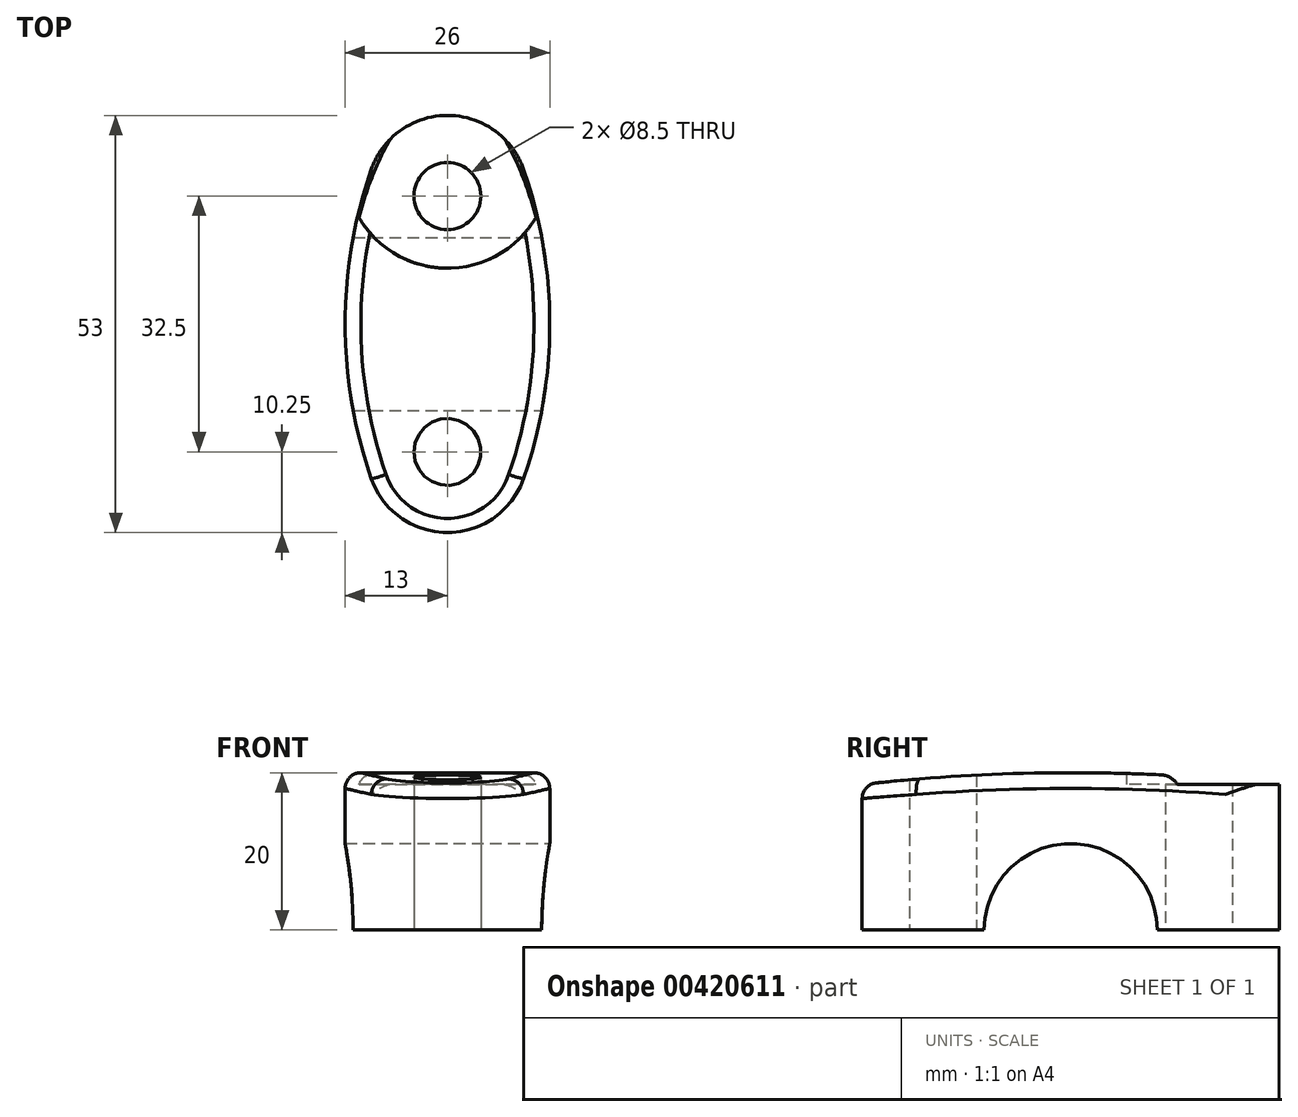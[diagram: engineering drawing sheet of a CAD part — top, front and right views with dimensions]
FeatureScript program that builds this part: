
annotation { "Feature Type Name" : "Feature", "Feature Type Description" : "" }
export const myFeature = defineFeature(function(context is Context, id is Id, definition is map)
    precondition{}
    {
        {
            var Q0;
            Q0=qCreatedBy(makeId("Top.planeOp"),FACE);
            var sketch = newSketch(context, id + "F0", { "sketchPlane" : qUnion([Q0])});
            skLineSegment(sketch, "E0.bottom", {"start": v(-13, 26.5) * mm, "end": v(13, 26.5) * mm, "construction": true});
            skLineSegment(sketch, "E0.top", {"start": v(-13, -26.5) * mm, "end": v(13, -26.5) * mm, "construction": true});
            skLineSegment(sketch, "E0.left", {"start": v(-13, 26.5) * mm, "end": v(-13, -26.5) * mm, "construction": true});
            skLineSegment(sketch, "E0.right", {"start": v(13, 26.5) * mm, "end": v(13, -26.5) * mm, "construction": true});
            skPoint(sketch, "E0.middle", {"position": v(0, 0) * mm});
            skArc(sketch, "E1", {"start": v(9.68, 19.62) * mm, "mid": v(0, 26.5) * mm, "end": v(-9.68, 19.62) * mm});
            skArc(sketch, "E2", {"start": v(-9.68, 19.62) * mm, "mid": v(-13, 0) * mm, "end": v(-9.68, -19.62) * mm});
            skArc(sketch, "E3", {"start": v(-9.68, -19.62) * mm, "mid": v(0, -26.5) * mm, "end": v(9.68, -19.62) * mm});
            skArc(sketch, "E4", {"start": v(9.68, -19.62) * mm, "mid": v(13, 0) * mm, "end": v(9.68, 19.62) * mm});
            skLineSegment(sketch, "E5", {"start": v(0, 16.25) * mm, "end": v(0, -16.25) * mm, "construction": true});
            skCircle(sketch, "E6", {"center": v(0, 16.25) * mm, "radius": 4.25 * mm});
            skCircle(sketch, "E7", {"center": v(0, -16.25) * mm, "radius": 4.25 * mm});
            skSolve(sketch);
        }
        {
            var Q0;
            Q0 = qSketchRegion(id + "F0", true);
            extrude(context, id + "F1", {"entities" : qUnion([Q0]), "depth" : 20 * mm, "offsetDistance" : 25 * mm});
        }
        {
            var Q0;
            Q0=qCreatedBy(makeId("Right.planeOp"),FACE);
            var sketch = newSketch(context, id + "F2", { "sketchPlane" : qUnion([Q0])});
            skCircle(sketch, "E8", {"center": v(0, 0) * mm, "radius": 11 * mm});
            skSolve(sketch);
        }
        {
            var Q0;
            Q0 = qSketchRegion(id + "F2", true);
            extrude(context, id + "F3", {"entities" : qUnion([Q0]), "operationType" : NewBodyOperationType.REMOVE, "oppositeDirection" : true, "depth" : 50 * mm, "offsetDistance" : 25 * mm, "symmetric" : true});
        }
        {
            var Q0;
            Q0=qCreatedBy(makeId("Right.planeOp"),FACE);
            var sketch = newSketch(context, id + "F4", { "sketchPlane" : qUnion([Q0])});
            skArc(sketch, "E9", {"start": v(26.5, 18.5) * mm, "mid": v(0, 20) * mm, "end": v(-26.5, 18.5) * mm});
            skLineSegment(sketch, "E10", {"start": v(-26.5, 18.5) * mm, "end": v(-26.5, 21) * mm});
            skLineSegment(sketch, "E11", {"start": v(-26.5, 21) * mm, "end": v(26.5, 21) * mm});
            skLineSegment(sketch, "E12", {"start": v(26.5, 21) * mm, "end": v(26.5, 18.5) * mm});
            skSolve(sketch);
        }
        {
            var Q0;
            Q0 = qSketchRegion(id + "F4", true);
            extrude(context, id + "F5", {"entities" : qUnion([Q0]), "operationType" : NewBodyOperationType.REMOVE, "oppositeDirection" : true, "depth" : 50 * mm, "offsetDistance" : 25 * mm, "symmetric" : true});
        }
        {
            var Q0;
            Q0=qCreatedBy(makeId("Top.planeOp"),FACE);
            cPlane(context, id + "F6", {"entities" : qUnion([Q0]), "cplaneType" : CPlaneType.OFFSET, "offset" : 18.5 * mm, "width" : 150 * mm, "height" : 150 * mm});
        }
        {
            var Q0;
            Q0=qCreatedBy(id+"F6.planeOp",FACE);
            var sketch = newSketch(context, id + "F7", { "sketchPlane" : qUnion([Q0])});
            skLineSegment(sketch, "E13.bottom", {"start": v(-11.38, 28.8) * mm, "end": v(11.38, 28.8) * mm});
            skLineSegment(sketch, "E13.left", {"start": v(-11.38, 28.8) * mm, "end": v(-11.38, 13.8) * mm});
            skLineSegment(sketch, "E13.right", {"start": v(11.38, 28.8) * mm, "end": v(11.38, 13.8) * mm});
            skArc(sketch, "E14", {"start": v(-11.38, 13.8) * mm, "mid": v(0, 7.08) * mm, "end": v(11.38, 13.8) * mm});
            skSolve(sketch);
        }
        {
            var Q0;
            Q0 = qSketchRegion(id + "F7", true);
            extrude(context, id + "F8", {"entities" : qUnion([Q0]), "operationType" : NewBodyOperationType.REMOVE, "endBound" : BoundingType.THROUGH_ALL, "depth" : 25 * mm, "offsetDistance" : 25 * mm});
        }
        {
            var Q0;
            Q0=makeQuery(id+"F5.boolean.opBoolean","INTERSECT",EDGE,{"derivedFrom":[makeQuery(id+"F1.opExtrude","SWEPT_FACE",FACE,{"disambiguationData":[OSD([sQuery(id+"F0.wireOp",EDGE,"E4")])]}),makeQuery(id+"F5.opExtrude","SWEPT_FACE",FACE,{"disambiguationData":[OSD([sQuery(id+"F4.wireOp",EDGE,"E9")])]})]});
            var Q1;
            Q1=makeQuery(id+"F5.boolean.opBoolean","INTERSECT",EDGE,{"derivedFrom":[makeQuery(id+"F1.opExtrude","SWEPT_FACE",FACE,{"disambiguationData":[OSD([sQuery(id+"F0.wireOp",EDGE,"E2")])]}),makeQuery(id+"F5.opExtrude","SWEPT_FACE",FACE,{"disambiguationData":[OSD([sQuery(id+"F4.wireOp",EDGE,"E9")])]})]});
            fillet(context, id + "F9", {"entities" : qUnion([Q0, Q1]), "radius" : 2 * mm, "tangentPropagation" : true, "allowEdgeOverflow" : false});
        }
    });
